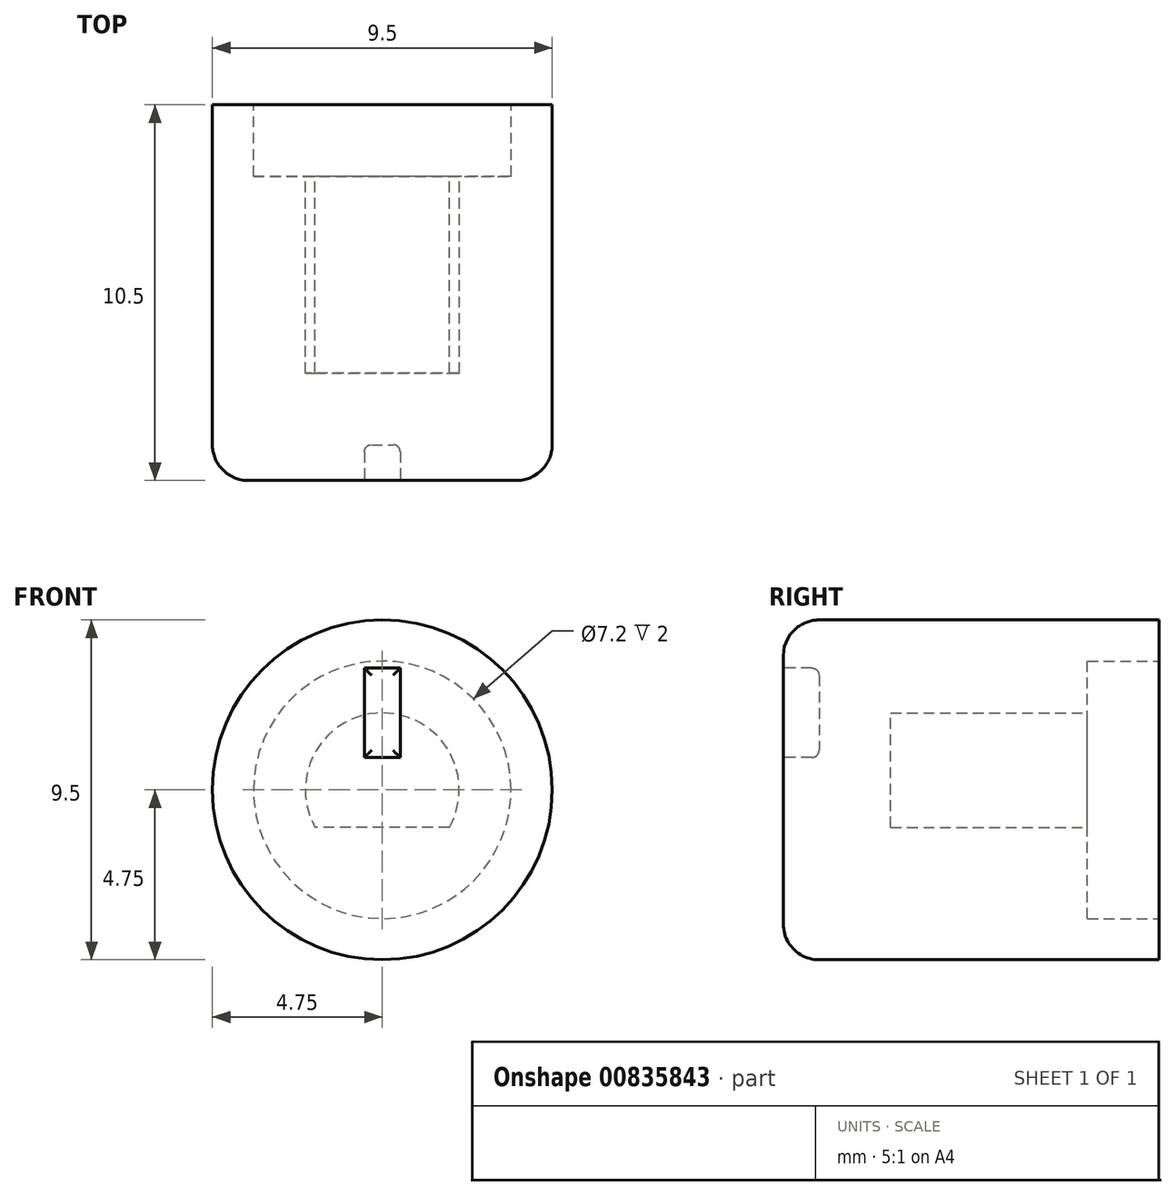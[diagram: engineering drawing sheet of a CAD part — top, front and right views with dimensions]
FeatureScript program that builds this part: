
annotation { "Feature Type Name" : "Feature", "Feature Type Description" : "" }
export const myFeature = defineFeature(function(context is Context, id is Id, definition is map)
    precondition{}
    {
        {
            var Q0;
            Q0=qCreatedBy(makeId("Front.planeOp"),FACE);
            var sketch = newSketch(context, id + "F0", { "sketchPlane" : qUnion([Q0])});
            skCircle(sketch, "E0", {"center": v(0, 0) * mm, "radius": 4.75 * mm});
            skCircle(sketch, "E1", {"center": v(0, 0) * mm, "radius": 3.6 * mm});
            skCircle(sketch, "E2", {"center": v(0, 0) * mm, "radius": 2.15 * mm});
            skLineSegment(sketch, "E3", {"start": v(-1.88, -1.05) * mm, "end": v(1.88, -1.05) * mm});
            skSolve(sketch);
        }
        {
            var Q0;
            {var subQ0=sQuery(id+"F0.wireOp",EDGE,"E3");Q0=makeQuery(id+"F0.imprint","IMPRINT",FACE,{"disambiguationData":[TD([[makeQuery(id+"F0.imprint","IMPRINT",EDGE,{"derivedFrom":subQ0}),1.0]])]});}
            var Q1;
            Q1=makeQuery(id+"F0.imprint","IMPRINT",FACE,{"disambiguationData":[TD([[makeQuery(id+"F0.imprint","IMPRINT",EDGE,{"derivedFrom":sQuery(id+"F0.wireOp",EDGE,"E1")}),1.0]])]});
            var Q2;
            {var subQ0=sQuery(id+"F0.wireOp",EDGE,"E3");Q2=makeQuery(id+"F0.imprint","IMPRINT",FACE,{"disambiguationData":[TD([[makeQuery(id+"F0.imprint","IMPRINT",EDGE,{"derivedFrom":subQ0}),-1.0]])]});}
            var Q3;
            Q3=makeQuery(id+"F0.imprint","IMPRINT",FACE,{"disambiguationData":[TD([[makeQuery(id+"F0.imprint","IMPRINT",EDGE,{"derivedFrom":sQuery(id+"F0.wireOp",EDGE,"E0")}),1.0]])]});
            extrude(context, id + "F1", {"entities" : qUnion([Q0, Q1, Q2, Q3]), "depth" : 10.5 * mm, "offsetDistance" : 25 * mm});
        }
        {
            var Q0;
            Q0=makeQuery(id+"F0.imprint","IMPRINT",FACE,{"disambiguationData":[TD([[makeQuery(id+"F0.imprint","IMPRINT",EDGE,{"derivedFrom":sQuery(id+"F0.wireOp",EDGE,"E1")}),1.0]])]});
            var Q1;
            {var subQ0=sQuery(id+"F0.wireOp",EDGE,"E3");Q1=makeQuery(id+"F0.imprint","IMPRINT",FACE,{"disambiguationData":[TD([[makeQuery(id+"F0.imprint","IMPRINT",EDGE,{"derivedFrom":subQ0}),1.0]])]});}
            var Q2;
            {var subQ0=sQuery(id+"F0.wireOp",EDGE,"E3");Q2=makeQuery(id+"F0.imprint","IMPRINT",FACE,{"disambiguationData":[TD([[makeQuery(id+"F0.imprint","IMPRINT",EDGE,{"derivedFrom":subQ0}),-1.0]])]});}
            extrude(context, id + "F2", {"entities" : qUnion([Q0, Q1, Q2]), "operationType" : NewBodyOperationType.REMOVE, "depth" : 2 * mm, "offsetDistance" : 25 * mm});
        }
        {
            var Q0;
            {var subQ0=sQuery(id+"F0.wireOp",EDGE,"E3");Q0=makeQuery(id+"F0.imprint","IMPRINT",FACE,{"disambiguationData":[TD([[makeQuery(id+"F0.imprint","IMPRINT",EDGE,{"derivedFrom":subQ0}),1.0]])]});}
            extrude(context, id + "F3", {"entities" : qUnion([Q0]), "operationType" : NewBodyOperationType.REMOVE, "depth" : 7.5 * mm, "offsetDistance" : 25 * mm});
        }
        {
            var Q0;
            Q0=makeQuery(id+"F1.opExtrude","CAP_FACE",FACE,{"disambiguationData":[OSD([sQuery(id+"F0.wireOp",EDGE,"E0")])],"isStart":false});
            var sketch = newSketch(context, id + "F4", { "sketchPlane" : qUnion([Q0])});
            skLineSegment(sketch, "E4.bottom", {"start": v(-0.5, 3.4) * mm, "end": v(0.5, 3.4) * mm});
            skLineSegment(sketch, "E4.top", {"start": v(-0.5, 0.9) * mm, "end": v(0.5, 0.9) * mm});
            skLineSegment(sketch, "E4.left", {"start": v(-0.5, 3.4) * mm, "end": v(-0.5, 0.9) * mm});
            skLineSegment(sketch, "E4.right", {"start": v(0.5, 3.4) * mm, "end": v(0.5, 0.9) * mm});
            skPoint(sketch, "E4.middle", {"position": v(0, 2.16) * mm});
            skSolve(sketch);
        }
        {
            var Q0;
            Q0=makeQuery(id+"F4.imprint","IMPRINT",FACE,{"disambiguationData":[TD([[makeQuery(id+"F4.imprint","IMPRINT",EDGE,{"derivedFrom":sQuery(id+"F4.wireOp",EDGE,"E4.bottom")}),-1.0]])]});
            extrude(context, id + "F5", {"entities" : qUnion([Q0]), "operationType" : NewBodyOperationType.REMOVE, "oppositeDirection" : true, "depth" : 1 * mm, "offsetDistance" : 25 * mm});
        }
        {
            var Q0;
            Q0=makeQuery(id+"F5.boolean.opBoolean","COPY",EDGE,{"derivedFrom":makeQuery(id+"F5.opExtrude","CAP_EDGE",EDGE,{"disambiguationData":[OSD([sQuery(id+"F4.wireOp",EDGE,"E4.left")])],"isStart":true})});
            var Q1;
            Q1=makeQuery(id+"F5.boolean.opBoolean","COPY",EDGE,{"derivedFrom":makeQuery(id+"F5.opExtrude","CAP_EDGE",EDGE,{"disambiguationData":[OSD([sQuery(id+"F4.wireOp",EDGE,"E4.bottom")])],"isStart":true})});
            var Q2;
            Q2=makeQuery(id+"F5.boolean.opBoolean","COPY",EDGE,{"derivedFrom":makeQuery(id+"F5.opExtrude","CAP_EDGE",EDGE,{"disambiguationData":[OSD([sQuery(id+"F4.wireOp",EDGE,"E4.right")])],"isStart":true})});
            var Q3;
            Q3=makeQuery(id+"F5.boolean.opBoolean","COPY",EDGE,{"derivedFrom":makeQuery(id+"F5.opExtrude","CAP_EDGE",EDGE,{"disambiguationData":[OSD([sQuery(id+"F4.wireOp",EDGE,"E4.top")])],"isStart":true})});
            var Q4;
            Q4=makeQuery(id+"F5.boolean.opBoolean","COPY",EDGE,{"derivedFrom":makeQuery(id+"F5.opExtrude","CAP_EDGE",EDGE,{"disambiguationData":[OSD([sQuery(id+"F4.wireOp",EDGE,"E4.bottom")])],"isStart":false})});
            var Q5;
            Q5=makeQuery(id+"F5.boolean.opBoolean","COPY",EDGE,{"derivedFrom":makeQuery(id+"F5.opExtrude","CAP_EDGE",EDGE,{"disambiguationData":[OSD([sQuery(id+"F4.wireOp",EDGE,"E4.right")])],"isStart":false})});
            var Q6;
            Q6=makeQuery(id+"F5.boolean.opBoolean","COPY",EDGE,{"derivedFrom":makeQuery(id+"F5.opExtrude","CAP_EDGE",EDGE,{"disambiguationData":[OSD([sQuery(id+"F4.wireOp",EDGE,"E4.left")])],"isStart":false})});
            var Q7;
            Q7=makeQuery(id+"F5.boolean.opBoolean","COPY",EDGE,{"derivedFrom":makeQuery(id+"F5.opExtrude","CAP_EDGE",EDGE,{"disambiguationData":[OSD([sQuery(id+"F4.wireOp",EDGE,"E4.top")])],"isStart":false})});
            fillet(context, id + "F6", {"entities" : qUnion([Q0, Q1, Q2, Q3, Q4, Q5, Q6, Q7]), "radius" : .2 * mm, "tangentPropagation" : true, "allowEdgeOverflow" : false});
        }
        {
            var Q0;
            Q0=makeQuery(id+"F1.opExtrude","CAP_EDGE",EDGE,{"disambiguationData":[OSD([sQuery(id+"F0.wireOp",EDGE,"E0")])],"isStart":false});
            fillet(context, id + "F7", {"entities" : qUnion([Q0]), "radius" : 1 * mm, "tangentPropagation" : true, "allowEdgeOverflow" : false});
        }
    });
